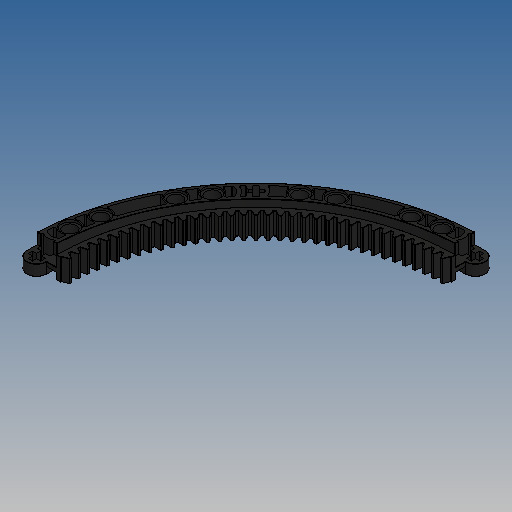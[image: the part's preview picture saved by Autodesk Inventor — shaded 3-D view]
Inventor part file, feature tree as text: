
AUTODESK INVENTOR PART (.ipt)
format: ipt  version: 2025 (Build 290162010, 162A)  size: 1,545,216 bytes
history: native  units: in
note: dims shown in document units (in); Inventor stores cm internally (conversion verified against a paired STEP export)
features: extrude x5, fillet x2, sketch x1, pattern_circular x1
ambient origin geometry x8: Origin, YZ Plane, XZ Plane, XY Plane, X Axis, Y Axis, Z Axis, Center Point
bodies: Solid1 (feature_tree)
feature tree (9):
  sketch  "Sketch2"  dims[d0=3.1496in d1=0.189in d2=0.2835in d3=0.189in d4=0.252in d5=0.315in d6=0.315in d8=45.0deg d10=0.4454in d11=0.4454in d12=0.1417in d13=0.0494in d14=0.0494in d15=0.0494in d16=0.1594in d17=0.1594in d18=0.1594in d19=0.063in d20=0.063in d21=0.4454in d22=2.8035in d23=2.8661in d24=0.0611in d25=0.0787in d26=0.0315in d27=0.0945in d28=0.1575in d29=0.0in d30=0.1575in d31=0.0in d32=0.063in d33=0.0in d34=0.252in d35=0.0in d36=0.315in d37=0.0in d38=0.0039in d39=13.7795in d40=0.6008in d42=0.063in d43=0.0039in d44=0.0157in d45=3.7795in]
  extrude  "Extrusion1"  Depth=0.0157in
  extrude  "Extrusion2"  Depth=0.0157in
  extrude  "Extrusion3"  Depth=0.0157in
  extrude  "Extrusion4"  Depth=0.0157in
  extrude  "Extrusion5"  Depth=0.0157in
  fillet  "Fillet1"  Radius=0.315in
  pattern_circular  "Circular Pattern1"  Angle=45.0deg  [1 undecoded]
  fillet  "Fillet2"  Radius=0.4454in
note: 1 required parameter value undecoded (feature->parameter linkage not recoverable at this tier; creation-order binding heuristic only, values carry confidence <= 0.55)
